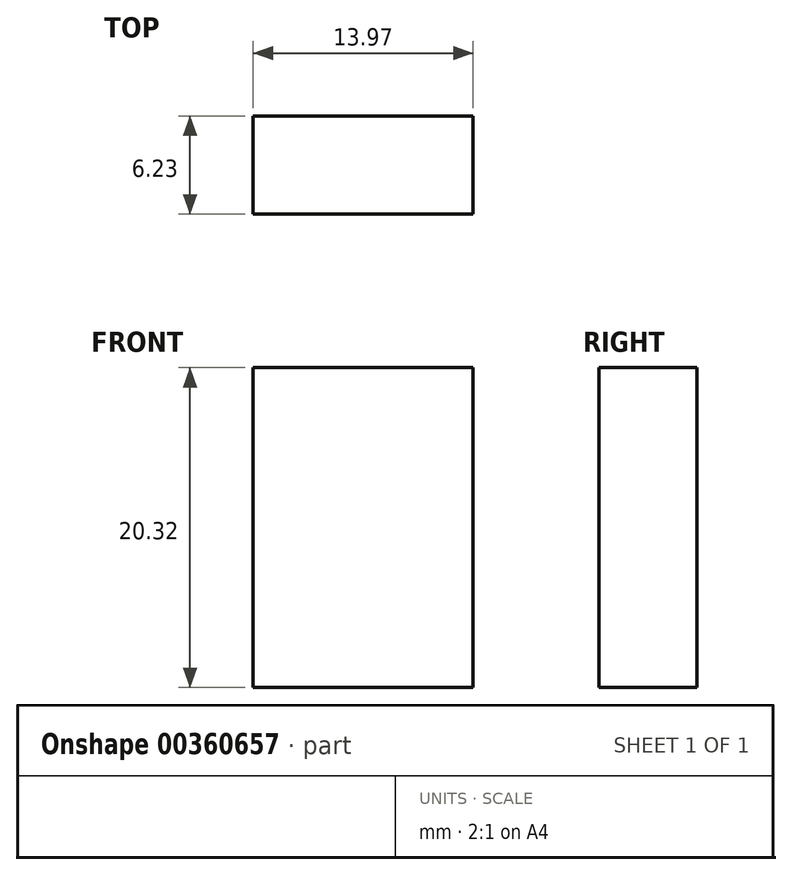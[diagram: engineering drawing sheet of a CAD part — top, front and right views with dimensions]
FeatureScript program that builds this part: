
annotation { "Feature Type Name" : "Feature", "Feature Type Description" : "" }
export const myFeature = defineFeature(function(context is Context, id is Id, definition is map)
    precondition{}
    {
        {
            var Q0;
            Q0=qCreatedBy(makeId("Right.planeOp"),FACE);
            var sketch = newSketch(context, id + "F0", { "sketchPlane" : qUnion([Q0])});
            skLineSegment(sketch, "E0.bottom", {"start": v(-42.42, -37.2) * mm, "end": v(-36.2, -37.2) * mm});
            skLineSegment(sketch, "E0.top", {"start": v(-42.42, -57.53) * mm, "end": v(-36.2, -57.53) * mm});
            skLineSegment(sketch, "E0.left", {"start": v(-42.42, -37.2) * mm, "end": v(-42.42, -57.53) * mm});
            skLineSegment(sketch, "E0.right", {"start": v(-36.2, -37.2) * mm, "end": v(-36.2, -57.53) * mm});
            skSolve(sketch);
        }
        {
            var Q0;
            Q0 = qSketchRegion(id + "F0", true);
            extrude(context, id + "F1", {"entities" : qUnion([Q0]), "depth" : 13.97 * mm});
        }
    });
